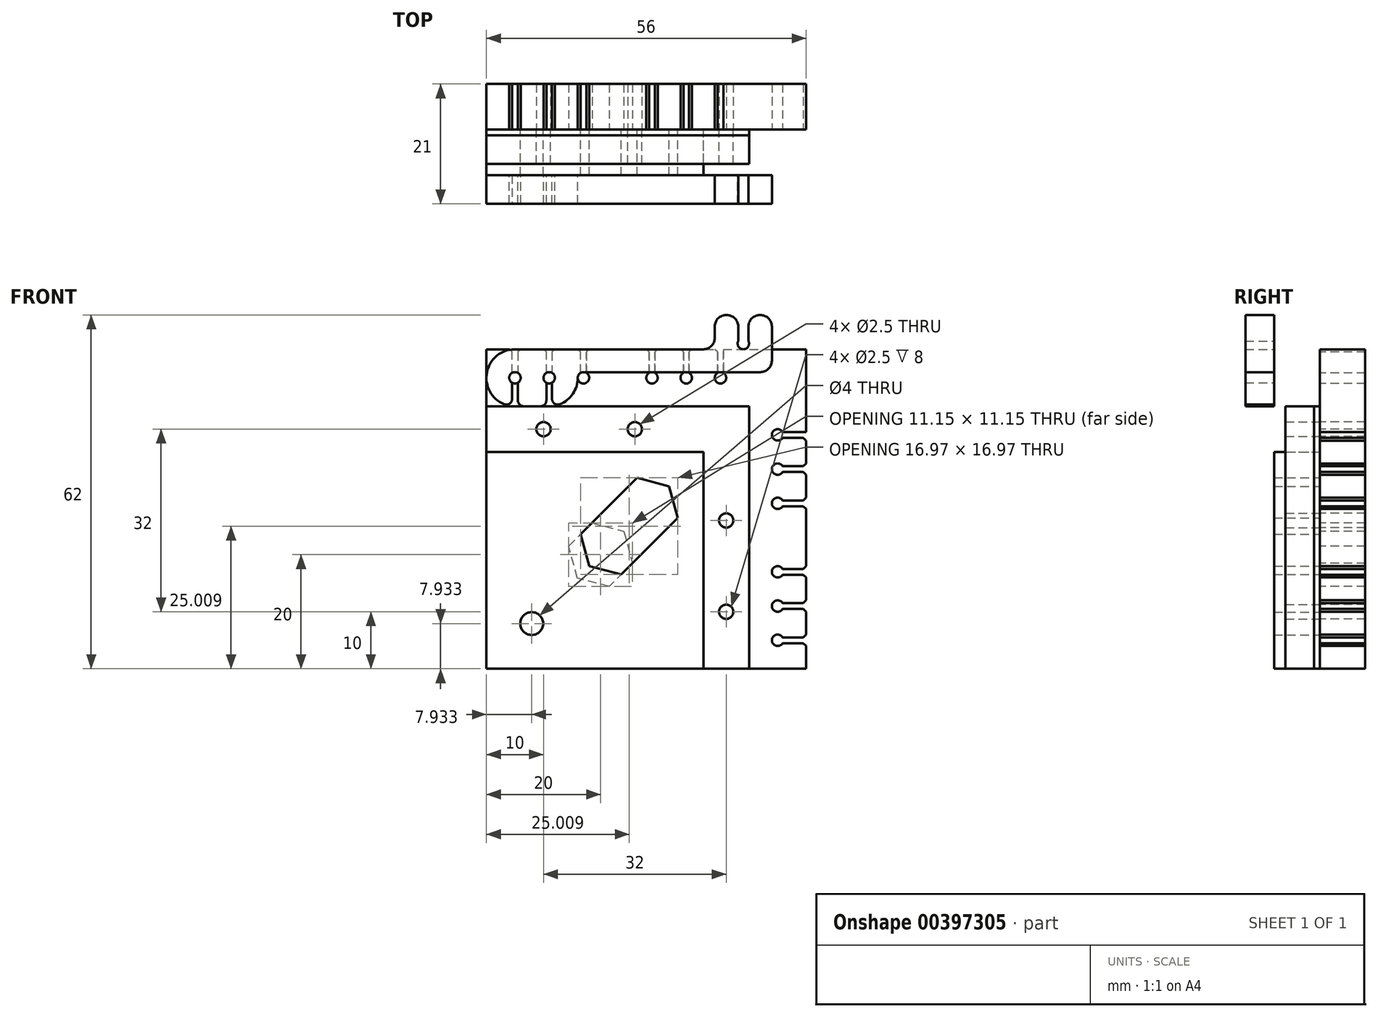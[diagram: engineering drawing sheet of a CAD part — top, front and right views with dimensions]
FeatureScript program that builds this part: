
annotation { "Feature Type Name" : "Feature", "Feature Type Description" : "" }
export const myFeature = defineFeature(function(context is Context, id is Id, definition is map)
    precondition{}
    {
        {
            assignVariable(context, id + "F0", {"name" : "Samm", "anyValue" : 4 * mm});
        }
        {
            assignVariable(context, id + "F1", {"name" : "Auk", "anyValue" : 2 * mm});
        }
        {
            assignVariable(context, id + "F2", {"name" : "Paksus", "anyValue" : getVariable(context, 'Samm') + getVariable(context, 'Auk') + getVariable(context, 'Samm') / 2});
        }
        {
            var Q0;
            Q0=qCreatedBy(makeId("Front.planeOp"),FACE);
            var sketch = newSketch(context, id + "F3", { "sketchPlane" : qUnion([Q0])});
            skLineSegment(sketch, "E0.bottom", {"start": v(0, 0) * mm, "end": v(56, 0) * mm});
            skLineSegment(sketch, "E0.top", {"start": v(0, 56) * mm, "end": v(56, 56) * mm});
            skLineSegment(sketch, "E0.left", {"start": v(0, 0) * mm, "end": v(0, 56) * mm});
            skLineSegment(sketch, "E0.right", {"start": v(56, 0) * mm, "end": v(56, 56) * mm});
            skLineSegment(sketch, "E1", {"start": v(0, 0) * mm, "end": v(56, 56) * mm});
            skLineSegment(sketch, "E2", {"start": v(0, 46) * mm, "end": v(46, 46) * mm});
            skLineSegment(sketch, "E3", {"start": v(0, 38) * mm, "end": v(38, 38) * mm});
            skLineSegment(sketch, "E4", {"start": v(0, 51) * mm, "end": v(56, 51) * mm, "construction": true});
            skLineSegment(sketch, "E5", {"start": v(46, 46) * mm, "end": v(46, 56) * mm, "construction": true});
            skLineSegment(sketch, "E6", {"start": v(38, 38) * mm, "end": v(38, 56) * mm, "construction": true});
            skLineSegment(sketch, "E7", {"start": v(0, 42) * mm, "end": v(42, 42) * mm, "construction": true});
            skPoint(sketch, "E8", {"position": v(26, 42) * mm});
            skPoint(sketch, "E9", {"position": v(10, 42) * mm});
            skSolve(sketch);
        }
        {
            var Q0;
            Q0=qCreatedBy(makeId("Front.planeOp"),FACE);
            var sketch = newSketch(context, id + "F4", { "sketchPlane" : qUnion([Q0])});
            skCircle(sketch, "E10", {"center": v(41, 51) * mm, "radius": 1 * mm});
            skCircle(sketch, "E11", {"center": v(35, 51) * mm, "radius": 1 * mm});
            skLineSegment(sketch, "E12", {"start": v(41.5, 56) * mm, "end": v(41.5, 51.87) * mm});
            skLineSegment(sketch, "E13.MirrorCS", {"start": v(40.5, 56) * mm, "end": v(40.5, 51.87) * mm});
            skLineSegment(sketch, "E14", {"start": v(40.5, 56) * mm, "end": v(41.5, 56) * mm});
            skCircle(sketch, "E15", {"center": v(29, 51) * mm, "radius": 1 * mm});
            skCircle(sketch, "E16", {"center": v(5, 51) * mm, "radius": 1 * mm});
            skLineSegment(sketch, "E17", {"start": v(5.5, 51.87) * mm, "end": v(5.5, 56) * mm});
            skLineSegment(sketch, "E18", {"start": v(5.5, 56) * mm, "end": v(4.5, 56) * mm});
            skLineSegment(sketch, "E19", {"start": v(4.5, 56) * mm, "end": v(4.5, 51.87) * mm});
            skCircle(sketch, "E20", {"center": v(11, 51) * mm, "radius": 1 * mm});
            skLineSegment(sketch, "E21", {"start": v(10.5, 56) * mm, "end": v(10.5, 51.87) * mm});
            skLineSegment(sketch, "E22", {"start": v(10.5, 56) * mm, "end": v(11.5, 56) * mm});
            skLineSegment(sketch, "E23", {"start": v(11.5, 51.87) * mm, "end": v(11.5, 56) * mm});
            skLineSegment(sketch, "E24", {"start": v(29.5, 51.87) * mm, "end": v(29.5, 56) * mm});
            skLineSegment(sketch, "E25", {"start": v(29.5, 56) * mm, "end": v(28.5, 56) * mm});
            skLineSegment(sketch, "E26", {"start": v(28.5, 56) * mm, "end": v(28.5, 51.87) * mm});
            skLineSegment(sketch, "E27", {"start": v(35.5, 51.87) * mm, "end": v(35.5, 56) * mm});
            skLineSegment(sketch, "E28", {"start": v(35.5, 56) * mm, "end": v(34.5, 56) * mm});
            skLineSegment(sketch, "E29", {"start": v(34.5, 56) * mm, "end": v(34.5, 51.87) * mm});
            skCircle(sketch, "E30", {"center": v(17, 51) * mm, "radius": 1 * mm});
            skLineSegment(sketch, "E31", {"start": v(16.5, 56) * mm, "end": v(16.5, 51.87) * mm});
            skLineSegment(sketch, "E32", {"start": v(16.5, 56) * mm, "end": v(17.5, 56) * mm});
            skLineSegment(sketch, "E33", {"start": v(17.5, 51.87) * mm, "end": v(17.5, 56) * mm});
            skSolve(sketch);
        }
        {
            var Q0;
            {var subQ3=sQuery(id+"F3.wireOp",EDGE,"E3");Q0=makeQuery(id+"F3.imprint","IMPRINT",FACE,{"disambiguationData":[TD([[makeQuery(id+"F3.imprint","IMPRINT",EDGE,{"derivedFrom":subQ3}),-1.0]])]});}
            var Q1;
            {var subQ0=sQuery(id+"F3.wireOp",EDGE,"E2");Q1=makeQuery(id+"F3.imprint","IMPRINT",FACE,{"disambiguationData":[TD([[makeQuery(id+"F3.imprint","IMPRINT",EDGE,{"derivedFrom":subQ0}),-1.0]])]});}
            var Q2;
            {var subQ7=sQuery(id+"F3.wireOp",EDGE,"E2");Q2=makeQuery(id+"F3.imprint","IMPRINT",FACE,{"disambiguationData":[TD([[makeQuery(id+"F3.imprint","IMPRINT",EDGE,{"derivedFrom":subQ7}),1.0]])]});}
            extrude(context, id + "F5", {"entities" : qUnion([Q0, Q1, Q2]), "oppositeDirection" : true, "depth" : 8 * mm});
        }
        {
            var Q0;
            {var subQ0=sQuery(id+"F3.wireOp",EDGE,"E2");Q0=makeQuery(id+"F3.imprint","IMPRINT",FACE,{"disambiguationData":[TD([[makeQuery(id+"F3.imprint","IMPRINT",EDGE,{"derivedFrom":subQ0}),-1.0]])]});}
            extrude(context, id + "F6", {"entities" : qUnion([Q0]), "depth" : 1 * mm});
        }
        {
            var Q0;
            {var subQ0=sQuery(id+"F4.wireOp",EDGE,"E16");var subQ1=makeQuery(id+"F4.imprint","INTERSECT",VERTEX,{"derivedFrom":[subQ0,sQuery(id+"F4.wireOp",EDGE,"E17")]});Q0=makeQuery(id+"F4.imprint","IMPRINT",FACE,{"disambiguationData":[TD([[makeQuery(id+"F4.imprint","IMPRINT",EDGE,{"disambiguationData":[TD([[subQ1,-1.0]])],"derivedFrom":subQ0}),1.0]])]});}
            var Q1;
            {var subQ0=sQuery(id+"F4.wireOp",EDGE,"E17");Q1=makeQuery(id+"F4.imprint","IMPRINT",FACE,{"disambiguationData":[TD([[makeQuery(id+"F4.imprint","IMPRINT",EDGE,{"derivedFrom":subQ0}),1.0]])]});}
            var Q2;
            {var subQ0=sQuery(id+"F4.wireOp",EDGE,"E20");var subQ1=makeQuery(id+"F4.imprint","INTERSECT",VERTEX,{"derivedFrom":[subQ0,sQuery(id+"F4.wireOp",EDGE,"E21")]});Q2=makeQuery(id+"F4.imprint","IMPRINT",FACE,{"disambiguationData":[TD([[makeQuery(id+"F4.imprint","IMPRINT",EDGE,{"disambiguationData":[TD([[subQ1,1.0]])],"derivedFrom":subQ0}),1.0]])]});}
            var Q3;
            {var subQ0=sQuery(id+"F4.wireOp",EDGE,"E21");Q3=makeQuery(id+"F4.imprint","IMPRINT",FACE,{"disambiguationData":[TD([[makeQuery(id+"F4.imprint","IMPRINT",EDGE,{"derivedFrom":subQ0}),1.0]])]});}
            var Q4;
            {var subQ0=sQuery(id+"F4.wireOp",EDGE,"QTqNx42c-BT7p-7A9X-RRYs-HgCFCDh2TXWR");Q4=makeQuery(id+"F4.imprint","IMPRINT",FACE,{"disambiguationData":[TD([[makeQuery(id+"F4.imprint","IMPRINT",EDGE,{"derivedFrom":subQ0}),1.0]])]});}
            var Q5;
            {var subQ0=sQuery(id+"F4.wireOp",EDGE,"DebvwMg3-Cwcg-wX2w-ogzT-Ep0VHspPX1UA");var subQ1=makeQuery(id+"F4.imprint","INTERSECT",VERTEX,{"derivedFrom":[subQ0,sQuery(id+"F4.wireOp",EDGE,"NG1M4aDK-SY8a-Geea-gYVj-s5fo7ngXQ215")]});Q5=makeQuery(id+"F4.imprint","IMPRINT",FACE,{"disambiguationData":[TD([[makeQuery(id+"F4.imprint","IMPRINT",EDGE,{"disambiguationData":[TD([[subQ1,-1.0]])],"derivedFrom":subQ0}),1.0]])]});}
            var Q6;
            {var subQ0=sQuery(id+"F4.wireOp",EDGE,"NG1M4aDK-SY8a-Geea-gYVj-s5fo7ngXQ215");Q6=makeQuery(id+"F4.imprint","IMPRINT",FACE,{"disambiguationData":[TD([[makeQuery(id+"F4.imprint","IMPRINT",EDGE,{"derivedFrom":subQ0}),1.0]])]});}
            var Q7;
            {var subQ0=sQuery(id+"F4.wireOp",EDGE,"E15");var subQ1=makeQuery(id+"F4.imprint","INTERSECT",VERTEX,{"derivedFrom":[subQ0,sQuery(id+"F4.wireOp",EDGE,"E24")]});Q7=makeQuery(id+"F4.imprint","IMPRINT",FACE,{"disambiguationData":[TD([[makeQuery(id+"F4.imprint","IMPRINT",EDGE,{"disambiguationData":[TD([[subQ1,-1.0]])],"derivedFrom":subQ0}),1.0]])]});}
            var Q8;
            {var subQ0=sQuery(id+"F4.wireOp",EDGE,"E24");Q8=makeQuery(id+"F4.imprint","IMPRINT",FACE,{"disambiguationData":[TD([[makeQuery(id+"F4.imprint","IMPRINT",EDGE,{"derivedFrom":subQ0}),1.0]])]});}
            var Q9;
            {var subQ0=sQuery(id+"F4.wireOp",EDGE,"E11");var subQ1=makeQuery(id+"F4.imprint","INTERSECT",VERTEX,{"derivedFrom":[subQ0,sQuery(id+"F4.wireOp",EDGE,"E27")]});Q9=makeQuery(id+"F4.imprint","IMPRINT",FACE,{"disambiguationData":[TD([[makeQuery(id+"F4.imprint","IMPRINT",EDGE,{"disambiguationData":[TD([[subQ1,-1.0]])],"derivedFrom":subQ0}),1.0]])]});}
            var Q10;
            {var subQ0=sQuery(id+"F4.wireOp",EDGE,"E27");Q10=makeQuery(id+"F4.imprint","IMPRINT",FACE,{"disambiguationData":[TD([[makeQuery(id+"F4.imprint","IMPRINT",EDGE,{"derivedFrom":subQ0}),1.0]])]});}
            var Q11;
            {var subQ0=sQuery(id+"F4.wireOp",EDGE,"E10");var subQ1=makeQuery(id+"F4.imprint","INTERSECT",VERTEX,{"derivedFrom":[subQ0,sQuery(id+"F4.wireOp",EDGE,"E12")]});Q11=makeQuery(id+"F4.imprint","IMPRINT",FACE,{"disambiguationData":[TD([[makeQuery(id+"F4.imprint","IMPRINT",EDGE,{"disambiguationData":[TD([[subQ1,-1.0]])],"derivedFrom":subQ0}),1.0]])]});}
            var Q12;
            {var subQ0=sQuery(id+"F4.wireOp",EDGE,"E12");Q12=makeQuery(id+"F4.imprint","IMPRINT",FACE,{"disambiguationData":[TD([[makeQuery(id+"F4.imprint","IMPRINT",EDGE,{"derivedFrom":subQ0}),-1.0]])]});}
            var Q13;
            {var subQ0=sQuery(id+"F4.wireOp",EDGE,"e30f7cc4-4558-49b8-8939-138344e96a64");Q13=makeQuery(id+"F4.imprint","IMPRINT",FACE,{"disambiguationData":[TD([[makeQuery(id+"F4.imprint","IMPRINT",EDGE,{"derivedFrom":subQ0}),-1.0]])]});}
            var Q14;
            {var subQ0=sQuery(id+"F4.wireOp",EDGE,"E31");Q14=makeQuery(id+"F4.imprint","IMPRINT",FACE,{"disambiguationData":[TD([[makeQuery(id+"F4.imprint","IMPRINT",EDGE,{"derivedFrom":subQ0}),1.0]])]});}
            var Q15;
            {var subQ0=sQuery(id+"F4.wireOp",EDGE,"E30");var subQ1=makeQuery(id+"F4.imprint","INTERSECT",VERTEX,{"derivedFrom":[subQ0,sQuery(id+"F4.wireOp",EDGE,"E31")]});Q15=makeQuery(id+"F4.imprint","IMPRINT",FACE,{"disambiguationData":[TD([[makeQuery(id+"F4.imprint","IMPRINT",EDGE,{"disambiguationData":[TD([[subQ1,1.0]])],"derivedFrom":subQ0}),1.0]])]});}
            extrude(context, id + "F7", {"entities" : qUnion([Q0, Q1, Q2, Q3, Q4, Q5, Q6, Q7, Q8, Q9, Q10, Q11, Q12, Q13, Q14, Q15]), "operationType" : NewBodyOperationType.REMOVE, "endBound" : BoundingType.UP_TO_NEXT, "oppositeDirection" : true, "depth" : 25 * mm});
        }
        {
            var Q0;
            Q0=makeQuery(id+"F7.boolean.opBoolean","COPY",EDGE,{"derivedFrom":makeQuery(id+"F7.opExtrude","SWEPT_EDGE",EDGE,{"disambiguationData":[OSD([sQuery(id+"F4.wireOp",EDGE,"E18"),sQuery(id+"F4.wireOp",EDGE,"E19")])]})});
            var Q1;
            Q1=makeQuery(id+"F7.boolean.opBoolean","COPY",EDGE,{"derivedFrom":makeQuery(id+"F7.opExtrude","SWEPT_EDGE",EDGE,{"disambiguationData":[OSD([sQuery(id+"F4.wireOp",EDGE,"E17"),sQuery(id+"F4.wireOp",EDGE,"E18")])]})});
            var Q2;
            Q2=makeQuery(id+"F7.boolean.opBoolean","COPY",EDGE,{"derivedFrom":makeQuery(id+"F7.opExtrude","SWEPT_EDGE",EDGE,{"disambiguationData":[OSD([sQuery(id+"F4.wireOp",EDGE,"E21"),sQuery(id+"F4.wireOp",EDGE,"E22")])]})});
            var Q3;
            Q3=makeQuery(id+"F7.boolean.opBoolean","COPY",EDGE,{"derivedFrom":makeQuery(id+"F7.opExtrude","SWEPT_EDGE",EDGE,{"disambiguationData":[OSD([sQuery(id+"F4.wireOp",EDGE,"E22"),sQuery(id+"F4.wireOp",EDGE,"E23")])]})});
            var Q4;
            Q4=makeQuery(id+"F7.boolean.opBoolean","COPY",EDGE,{"derivedFrom":makeQuery(id+"F7.opExtrude","SWEPT_EDGE",EDGE,{"disambiguationData":[OSD([sQuery(id+"F4.wireOp",EDGE,"E13.MirrorCS"),sQuery(id+"F4.wireOp",EDGE,"E14")])]})});
            var Q5;
            Q5=makeQuery(id+"F7.boolean.opBoolean","COPY",EDGE,{"derivedFrom":makeQuery(id+"F7.opExtrude","SWEPT_EDGE",EDGE,{"disambiguationData":[OSD([sQuery(id+"F4.wireOp",EDGE,"E12"),sQuery(id+"F4.wireOp",EDGE,"E14")])]})});
            var Q6;
            Q6=makeQuery(id+"F7.boolean.opBoolean","COPY",EDGE,{"derivedFrom":makeQuery(id+"F7.opExtrude","SWEPT_EDGE",EDGE,{"disambiguationData":[OSD([sQuery(id+"F4.wireOp",EDGE,"E27"),sQuery(id+"F4.wireOp",EDGE,"E28")])]})});
            var Q7;
            Q7=makeQuery(id+"F7.boolean.opBoolean","COPY",EDGE,{"derivedFrom":makeQuery(id+"F7.opExtrude","SWEPT_EDGE",EDGE,{"disambiguationData":[OSD([sQuery(id+"F4.wireOp",EDGE,"E28"),sQuery(id+"F4.wireOp",EDGE,"E29")])]})});
            var Q8;
            Q8=makeQuery(id+"F7.boolean.opBoolean","COPY",EDGE,{"derivedFrom":makeQuery(id+"F7.opExtrude","SWEPT_EDGE",EDGE,{"disambiguationData":[OSD([sQuery(id+"F4.wireOp",EDGE,"E24"),sQuery(id+"F4.wireOp",EDGE,"E25")])]})});
            var Q9;
            Q9=makeQuery(id+"F7.boolean.opBoolean","COPY",EDGE,{"derivedFrom":makeQuery(id+"F7.opExtrude","SWEPT_EDGE",EDGE,{"disambiguationData":[OSD([sQuery(id+"F4.wireOp",EDGE,"E25"),sQuery(id+"F4.wireOp",EDGE,"E26")])]})});
            var Q10;
            Q10=makeQuery(id+"F7.boolean.opBoolean","COPY",EDGE,{"derivedFrom":makeQuery(id+"F7.opExtrude","SWEPT_EDGE",EDGE,{"disambiguationData":[OSD([sQuery(id+"F4.wireOp",EDGE,"E31"),sQuery(id+"F4.wireOp",EDGE,"E32")])]})});
            var Q11;
            Q11=makeQuery(id+"F7.boolean.opBoolean","COPY",EDGE,{"derivedFrom":makeQuery(id+"F7.opExtrude","SWEPT_EDGE",EDGE,{"disambiguationData":[OSD([sQuery(id+"F4.wireOp",EDGE,"E32"),sQuery(id+"F4.wireOp",EDGE,"E33")])]})});
            chamfer(context, id + "F8", {"entities" : qUnion([Q0, Q1, Q2, Q3, Q4, Q5, Q6, Q7, Q8, Q9, Q10, Q11]), "width" : 0.5 * mm, "tangentPropagation" : true});
        }
        {
            var Q0;
            Q0=sQuery(id+"F3.wireOp",VERTEX,"E9");
            var Q1;
            Q1=sQuery(id+"F3.wireOp",VERTEX,"E8");
            var Q2;
            Q2=makeQuery(id+"F5.opExtrude","SWEPT_BODY",BODY,{"disambiguationData":[OSD([sQuery(id+"F3.wireOp",EDGE,"E0.top"),sQuery(id+"F3.wireOp",EDGE,"E0.left"),sQuery(id+"F3.wireOp",EDGE,"E1")])]});
            hole(context, id + "F9", {"style" : HoleStyle.SIMPLE, "endStyle" : HoleEndStyle.THROUGH, "holeDiameter" : 2.5 * mm, "isTappedThrough" : true, "tappedDepth" : 12 * mm, "tapClearance" : 3, "locations" : qUnion([Q0, Q1]), "scope" : qUnion([Q2])});
        }
        {
            var Q0;
            Q0=makeQuery(id+"F5.opExtrude","SWEPT_BODY",BODY,{"disambiguationData":[OSD([sQuery(id+"F3.wireOp",EDGE,"E0.top"),sQuery(id+"F3.wireOp",EDGE,"E0.left"),sQuery(id+"F3.wireOp",EDGE,"E1")])]});
            var Q1;
            Q1=makeQuery(id+"F5.opExtrude","SWEPT_FACE",FACE,{"disambiguationData":[OSD([sQuery(id+"F3.wireOp",EDGE,"E1")])]});
            mirror(context, id + "F10", {"operationType" : NewBodyOperationType.ADD, "entities" : qUnion([Q0]), "mirrorPlane" : qUnion([Q1])});
        }
        {
            var Q0;
            Q0=makeQuery(id+"F6.opExtrude","SWEPT_BODY",BODY,{"disambiguationData":[OSD([sQuery(id+"F3.wireOp",EDGE,"E0.left"),sQuery(id+"F3.wireOp",EDGE,"E1"),sQuery(id+"F3.wireOp",EDGE,"E2"),sQuery(id+"F3.wireOp",EDGE,"E3")])]});
            var Q1;
            Q1=makeQuery(id+"F6.opExtrude","SWEPT_FACE",FACE,{"disambiguationData":[OSD([sQuery(id+"F3.wireOp",EDGE,"E1")])]});
            mirror(context, id + "F11", {"operationType" : NewBodyOperationType.ADD, "entities" : qUnion([Q0]), "mirrorPlane" : qUnion([Q1])});
        }
        {
            var Q0;
            {var subQ3=sQuery(id+"F3.wireOp",EDGE,"E3");Q0=makeQuery(id+"F3.imprint","IMPRINT",FACE,{"disambiguationData":[TD([[makeQuery(id+"F3.imprint","IMPRINT",EDGE,{"derivedFrom":subQ3}),-1.0]])]});}
            var sketch = newSketch(context, id + "F12", { "sketchPlane" : qUnion([Q0])});
            skLineSegment(sketch, "E34.0", {"start": v(0, 38) * mm, "end": v(38, 38) * mm});
            skLineSegment(sketch, "E35.0", {"start": v(38, 0) * mm, "end": v(38, 38) * mm});
            skLineSegment(sketch, "E36.0", {"start": v(0, 0) * mm, "end": v(0, 56) * mm});
            skLineSegment(sketch, "E37.0", {"start": v(0, 0) * mm, "end": v(56, 0) * mm});
            skLineSegment(sketch, "E38.0", {"start": v(0, 0) * mm, "end": v(56, 56) * mm});
            skLineSegment(sketch, "E39", {"start": v(32, 32) * mm, "end": v(26.42, 33.5) * mm});
            skLineSegment(sketch, "E40", {"start": v(26.42, 33.5) * mm, "end": v(16.52, 23.6) * mm});
            skLineSegment(sketch, "E41", {"start": v(16.52, 23.6) * mm, "end": v(18.02, 18.02) * mm});
            skLineSegment(sketch, "E42.MirrorCS", {"start": v(23.6, 16.52) * mm, "end": v(18.02, 18.02) * mm});
            skLineSegment(sketch, "E43.MirrorCS", {"start": v(32, 32) * mm, "end": v(33.5, 26.42) * mm});
            skLineSegment(sketch, "E44.MirrorCS", {"start": v(33.5, 26.42) * mm, "end": v(23.6, 16.52) * mm});
            skPoint(sketch, "E45", {"position": v(7.93, 7.93) * mm});
            skSolve(sketch);
        }
        {
            var Q0;
            Q0=qSketchRegion(id+"F12",true);
            extrude(context, id + "F13", {"entities" : qUnion([Q0]), "depth" : getVariable(context, 'Paksus')});
        }
        {
            var Q0;
            Q0=makeQuery(id+"F13.opExtrude","CAP_FACE",FACE,{"disambiguationData":[OSD([sQuery(id+"F12.wireOp",EDGE,"E34.0"),sQuery(id+"F12.wireOp",EDGE,"E35.0"),sQuery(id+"F12.wireOp",EDGE,"E36.0"),sQuery(id+"F12.wireOp",EDGE,"E37.0"),sQuery(id+"F12.wireOp",EDGE,"2cf8d3c9-5500-4004-992a-a7f99b6d44c5.0"),sQuery(id+"F12.wireOp",EDGE,"2cf8d3c9-5500-4004-992a-a7f99b6d44c5.1"),sQuery(id+"F12.wireOp",EDGE,"2cf8d3c9-5500-4004-992a-a7f99b6d44c5.2"),sQuery(id+"F12.wireOp",EDGE,"2cf8d3c9-5500-4004-992a-a7f99b6d44c5.3"),sQuery(id+"F12.wireOp",EDGE,"2cf8d3c9-5500-4004-992a-a7f99b6d44c5.4"),sQuery(id+"F12.wireOp",EDGE,"2cf8d3c9-5500-4004-992a-a7f99b6d44c5.5")])],"isStart":false});
            var sketch = newSketch(context, id + "F14", { "sketchPlane" : qUnion([Q0])});
            skCircle(sketch, "E46.0", {"center": v(5, 51) * mm, "radius": 1 * mm});
            skCircle(sketch, "E47.0", {"center": v(11, 51) * mm, "radius": 1 * mm});
            skCircle(sketch, "E48.0", {"center": v(41, 51) * mm, "radius": 1 * mm});
            skCircle(sketch, "E49", {"center": v(11, 51) * mm, "radius": 5 * mm});
            skCircle(sketch, "E50", {"center": v(5, 51) * mm, "radius": 5 * mm});
            skLineSegment(sketch, "E51.0", {"start": v(0, 51) * mm, "end": v(56, 51) * mm, "construction": true});
            skCircle(sketch, "E52", {"center": v(45, 57) * mm, "radius": 1 * mm});
            skLineSegment(sketch, "E53", {"start": v(50, 52) * mm, "end": v(15.9, 52) * mm});
            skLineSegment(sketch, "E54", {"start": v(4.5, 50.13) * mm, "end": v(4.5, 46.03) * mm});
            skLineSegment(sketch, "E55", {"start": v(5.5, 50.13) * mm, "end": v(5.5, 46.03) * mm});
            skLineSegment(sketch, "E56", {"start": v(10.5, 50.13) * mm, "end": v(10.5, 46.03) * mm});
            skLineSegment(sketch, "E57", {"start": v(11.5, 50.13) * mm, "end": v(11.5, 46.03) * mm});
            skLineSegment(sketch, "E58", {"start": v(5.5, 46.03) * mm, "end": v(10.5, 46.03) * mm});
            skLineSegment(sketch, "E59.0", {"start": v(46, 46) * mm, "end": v(46, 56) * mm, "construction": true});
            skLineSegment(sketch, "E60", {"start": v(45.9, 57.44) * mm, "end": v(45.9, 62) * mm});
            skLineSegment(sketch, "E61", {"start": v(44.1, 57.44) * mm, "end": v(44.1, 62) * mm});
            skLineSegment(sketch, "E62", {"start": v(50, 52) * mm, "end": v(50, 62) * mm});
            skLineSegment(sketch, "E63", {"start": v(50, 62) * mm, "end": v(40, 62) * mm});
            skLineSegment(sketch, "E64", {"start": v(40, 62) * mm, "end": v(40, 56) * mm});
            skLineSegment(sketch, "E65", {"start": v(40, 56) * mm, "end": v(5, 56) * mm});
            skPoint(sketch, "E66.orphan", {"position": v(0, 62) * mm});
            skPoint(sketch, "E67.start.orphan", {"position": v(0, 56) * mm});
            skSolve(sketch);
        }
        {
            var Q0;
            {var subQ0=sQuery(id+"F14.wireOp",EDGE,"E56");Q0=makeQuery(id+"F14.imprint","IMPRINT",FACE,{"disambiguationData":[TD([[makeQuery(id+"F14.imprint","IMPRINT",EDGE,{"derivedFrom":subQ0}),-1.0]])]});}
            var Q1;
            {var subQ0=sQuery(id+"F14.wireOp",EDGE,"AxJx2oVJ-XFwZ-MC76-LPeR-xshG9jsGcbUg");var subQ1=sQuery(id+"F14.wireOp",EDGE,"E49");var subQ2=makeQuery(id+"F14.imprint","INTERSECT",VERTEX,{"derivedFrom":[subQ1,subQ0]});Q1=makeQuery(id+"F14.imprint","IMPRINT",FACE,{"disambiguationData":[TD([[makeQuery(id+"F14.imprint","IMPRINT",EDGE,{"disambiguationData":[TD([[subQ2,-1.0]])],"derivedFrom":subQ1}),-1.0]])]});}
            var Q2;
            {var subQ0=sQuery(id+"F14.wireOp",EDGE,"E58");Q2=makeQuery(id+"F14.imprint","IMPRINT",FACE,{"disambiguationData":[TD([[makeQuery(id+"F14.imprint","IMPRINT",EDGE,{"derivedFrom":subQ0}),1.0]])]});}
            var Q3;
            {var subQ0=sQuery(id+"F14.wireOp",EDGE,"CSsFTJs7-Jaks-gvLE-uZ3l-TUTck8eSOqBI");Q3=makeQuery(id+"F14.imprint","IMPRINT",FACE,{"disambiguationData":[TD([[makeQuery(id+"F14.imprint","IMPRINT",EDGE,{"derivedFrom":subQ0}),-1.0]])]});}
            var Q4;
            {var subQ2=sQuery(id+"F14.wireOp",EDGE,"E54");Q4=makeQuery(id+"F14.imprint","IMPRINT",FACE,{"disambiguationData":[TD([[makeQuery(id+"F14.imprint","IMPRINT",EDGE,{"derivedFrom":subQ2}),-1.0]])]});}
            var Q5;
            {var subQ2=sQuery(id+"F14.wireOp",EDGE,"E57");Q5=makeQuery(id+"F14.imprint","IMPRINT",FACE,{"disambiguationData":[TD([[makeQuery(id+"F14.imprint","IMPRINT",EDGE,{"derivedFrom":subQ2}),1.0]])]});}
            var Q6;
            {var subQ6=sQuery(id+"F14.wireOp",EDGE,"E60");var subQ8=sQuery(id+"F14.wireOp",EDGE,"E52");var subQ9=makeQuery(id+"F14.imprint","INTERSECT",VERTEX,{"derivedFrom":[subQ8,subQ6]});Q6=makeQuery(id+"F14.imprint","IMPRINT",FACE,{"disambiguationData":[TD([[makeQuery(id+"F14.imprint","IMPRINT",EDGE,{"disambiguationData":[TD([[subQ9,1.0]])],"derivedFrom":subQ8}),-1.0]])]});}
            var Q7;
            {var subQ0=sQuery(id+"F14.wireOp",EDGE,"E55");Q7=makeQuery(id+"F14.imprint","IMPRINT",FACE,{"disambiguationData":[TD([[makeQuery(id+"F14.imprint","IMPRINT",EDGE,{"derivedFrom":subQ0}),1.0]])]});}
            var Q8;
            {var subQ0=sQuery(id+"F14.wireOp",EDGE,"E55");Q8=makeQuery(id+"F14.imprint","IMPRINT",FACE,{"disambiguationData":[TD([[makeQuery(id+"F14.imprint","IMPRINT",EDGE,{"derivedFrom":subQ0}),1.0]])]});}
            var Q9;
            {var subQ0=sQuery(id+"F14.wireOp",EDGE,"E56");Q9=makeQuery(id+"F14.imprint","IMPRINT",FACE,{"disambiguationData":[TD([[makeQuery(id+"F14.imprint","IMPRINT",EDGE,{"derivedFrom":subQ0}),-1.0]])]});}
            var Q10;
            {var subQ0=sQuery(id+"F14.wireOp",EDGE,"E53");var subQ1=sQuery(id+"F14.wireOp",EDGE,"E49");var subQ2=makeQuery(id+"F14.imprint","INTERSECT",VERTEX,{"derivedFrom":[subQ1,subQ0]});Q10=makeQuery(id+"F14.imprint","IMPRINT",FACE,{"disambiguationData":[TD([[makeQuery(id+"F14.imprint","IMPRINT",EDGE,{"disambiguationData":[TD([[subQ2,-1.0]])],"derivedFrom":subQ1}),-1.0]])]});}
            var Q11;
            {var subQ0=sQuery(id+"F14.wireOp",EDGE,"E49");var subQ1=makeQuery(id+"F14.imprint","INTERSECT",VERTEX,{"derivedFrom":[sQuery(id+"F14.wireOp",EDGE,"E46.0"),subQ0]});Q11=makeQuery(id+"F14.imprint","IMPRINT",FACE,{"disambiguationData":[TD([[makeQuery(id+"F14.imprint","IMPRINT",EDGE,{"disambiguationData":[TD([[subQ1,1.0]])],"derivedFrom":subQ0}),1.0]])]});}
            var Q12;
            {var subQ0=sQuery(id+"F14.wireOp",EDGE,"E49");var subQ1=makeQuery(id+"F14.imprint","INTERSECT",VERTEX,{"derivedFrom":[sQuery(id+"F14.wireOp",EDGE,"E46.0"),subQ0]});Q12=makeQuery(id+"F14.imprint","IMPRINT",FACE,{"disambiguationData":[TD([[makeQuery(id+"F14.imprint","IMPRINT",EDGE,{"disambiguationData":[TD([[subQ1,1.0]])],"derivedFrom":subQ0}),1.0]])]});}
            var Q13;
            {var subQ2=sQuery(id+"F14.wireOp",EDGE,"E54");Q13=makeQuery(id+"F14.imprint","IMPRINT",FACE,{"disambiguationData":[TD([[makeQuery(id+"F14.imprint","IMPRINT",EDGE,{"derivedFrom":subQ2}),-1.0]])]});}
            var Q14;
            {var subQ0=sQuery(id+"F14.wireOp",EDGE,"BxTuXfEc-kO9Q-QHb8-LTs3-kqM6wV0efrVW");var subQ1=sQuery(id+"F14.wireOp",EDGE,"E48.0");var subQ2=makeQuery(id+"F14.imprint","INTERSECT",VERTEX,{"derivedFrom":[subQ1,subQ0]});Q14=makeQuery(id+"F14.imprint","IMPRINT",FACE,{"disambiguationData":[TD([[makeQuery(id+"F14.imprint","IMPRINT",EDGE,{"disambiguationData":[TD([[subQ2,-1.0]])],"derivedFrom":subQ1}),-1.0]])]});}
            extrude(context, id + "F15", {"entities" : qUnion([Q0, Q1, Q2, Q3, Q4, Q5, Q6, Q7, Q8, Q9, Q10, Q11, Q12, Q13, Q14]), "depth" : 5 * mm});
        }
        {
            var Q0;
            Q0=makeQuery(id+"F15.opExtrude","SWEPT_EDGE",EDGE,{"disambiguationData":[OSD([sQuery(id+"F14.wireOp",EDGE,"E50"),sQuery(id+"F14.wireOp",EDGE,"E54")])]});
            var Q1;
            Q1=makeQuery(id+"F15.opExtrude","SWEPT_EDGE",EDGE,{"disambiguationData":[OSD([sQuery(id+"F14.wireOp",EDGE,"E50"),sQuery(id+"F14.wireOp",EDGE,"E55"),sQuery(id+"F14.wireOp",EDGE,"E58")])]});
            var Q2;
            Q2=makeQuery(id+"F15.opExtrude","SWEPT_EDGE",EDGE,{"disambiguationData":[OSD([sQuery(id+"F14.wireOp",EDGE,"E49"),sQuery(id+"F14.wireOp",EDGE,"E56"),sQuery(id+"F14.wireOp",EDGE,"E58")])]});
            var Q3;
            Q3=makeQuery(id+"F15.opExtrude","SWEPT_EDGE",EDGE,{"disambiguationData":[OSD([sQuery(id+"F14.wireOp",EDGE,"E49"),sQuery(id+"F14.wireOp",EDGE,"E57")])]});
            var Q4;
            Q4=makeQuery(id+"F15.opExtrude","SWEPT_EDGE",EDGE,{"disambiguationData":[OSD([sQuery(id+"F14.wireOp",EDGE,"AxJx2oVJ-XFwZ-MC76-LPeR-xshG9jsGcbUg"),sQuery(id+"F14.wireOp",EDGE,"ckgy3OCV-uk7f-uJ41-MpvO-jaV0Tc8mXzn0")])]});
            var Q5;
            Q5=makeQuery(id+"F15.opExtrude","SWEPT_EDGE",EDGE,{"disambiguationData":[OSD([sQuery(id+"F14.wireOp",EDGE,"AxJx2oVJ-XFwZ-MC76-LPeR-xshG9jsGcbUg"),sQuery(id+"F14.wireOp",EDGE,"Tde4fxld-xR9Y-IW79-mpMQ-LUkHlr8zzJhR")])]});
            var Q6;
            Q6=makeQuery(id+"F15.opExtrude","SWEPT_EDGE",EDGE,{"disambiguationData":[OSD([sQuery(id+"F14.wireOp",EDGE,"E49"),sQuery(id+"F14.wireOp",EDGE,"E53")])]});
            fillet(context, id + "F16", {"entities" : qUnion([Q0, Q1, Q2, Q3, Q4, Q5, Q6]), "radius" : 1 * mm, "tangentPropagation" : true, "allowEdgeOverflow" : false});
        }
        {
            var Q0;
            Q0=sQuery(id+"F12.wireOp",VERTEX,"E45");
            var Q1;
            Q1=makeQuery(id+"F13.opExtrude","SWEPT_BODY",BODY,{"disambiguationData":[OSD([sQuery(id+"F12.wireOp",EDGE,"E34.0"),sQuery(id+"F12.wireOp",EDGE,"E35.0"),sQuery(id+"F12.wireOp",EDGE,"E36.0"),sQuery(id+"F12.wireOp",EDGE,"E37.0"),sQuery(id+"F12.wireOp",EDGE,"E39"),sQuery(id+"F12.wireOp",EDGE,"E40"),sQuery(id+"F12.wireOp",EDGE,"E41"),sQuery(id+"F12.wireOp",EDGE,"E42.MirrorCS"),sQuery(id+"F12.wireOp",EDGE,"E44.MirrorCS"),sQuery(id+"F12.wireOp",EDGE,"E43.MirrorCS")])]});
            hole(context, id + "F17", {"style" : HoleStyle.SIMPLE, "endStyle" : HoleEndStyle.THROUGH, "oppositeDirection" : true, "holeDiameter" : 4 * mm, "isTappedThrough" : true, "tappedDepth" : 12 * mm, "tapClearance" : 3, "locations" : qUnion([Q0]), "scope" : qUnion([Q1])});
        }
        {
            var Q0;
            Q0=makeQuery(id+"F15.opExtrude","SWEPT_EDGE",EDGE,{"disambiguationData":[OSD([sQuery(id+"F14.wireOp",EDGE,"E64"),sQuery(id+"F14.wireOp",EDGE,"E65")])]});
            var Q1;
            Q1=makeQuery(id+"F15.opExtrude","SWEPT_EDGE",EDGE,{"disambiguationData":[OSD([sQuery(id+"F14.wireOp",EDGE,"E63"),sQuery(id+"F14.wireOp",EDGE,"E64")])]});
            var Q2;
            Q2=makeQuery(id+"F15.opExtrude","SWEPT_EDGE",EDGE,{"disambiguationData":[OSD([sQuery(id+"F14.wireOp",EDGE,"E61"),sQuery(id+"F14.wireOp",EDGE,"E63")])]});
            var Q3;
            Q3=makeQuery(id+"F15.opExtrude","SWEPT_EDGE",EDGE,{"disambiguationData":[OSD([sQuery(id+"F14.wireOp",EDGE,"E60"),sQuery(id+"F14.wireOp",EDGE,"E63")])]});
            var Q4;
            Q4=makeQuery(id+"F15.opExtrude","SWEPT_EDGE",EDGE,{"disambiguationData":[OSD([sQuery(id+"F14.wireOp",EDGE,"E62"),sQuery(id+"F14.wireOp",EDGE,"E63")])]});
            var Q5;
            Q5=makeQuery(id+"F15.opExtrude","SWEPT_EDGE",EDGE,{"disambiguationData":[OSD([sQuery(id+"F14.wireOp",EDGE,"E53"),sQuery(id+"F14.wireOp",EDGE,"E62")])]});
            fillet(context, id + "F18", {"entities" : qUnion([Q0, Q1, Q2, Q3, Q4, Q5]), "radius" : 2 * mm, "tangentPropagation" : true, "allowEdgeOverflow" : false});
        }
        {
            var Q0;
            {var subQ3=sQuery(id+"F3.wireOp",EDGE,"E0.bottom");Q0=makeQuery(id+"F3.imprint","IMPRINT",FACE,{"disambiguationData":[TD([[makeQuery(id+"F3.imprint","IMPRINT",EDGE,{"derivedFrom":subQ3}),1.0]])]});}
            var sketch = newSketch(context, id + "F19", { "sketchPlane" : qUnion([Q0])});
            skCircle(sketch, "E68.cCircle", {"center": v(20, 20) * mm, "radius": 5.77 * mm, "construction": true});
            skLineSegment(sketch, "E68.0", {"start": v(25.58, 18.5) * mm, "end": v(21.5, 14.42) * mm});
            skLineSegment(sketch, "E68.1", {"start": v(21.5, 14.42) * mm, "end": v(15.92, 15.92) * mm});
            skLineSegment(sketch, "E68.2", {"start": v(15.92, 15.92) * mm, "end": v(14.42, 21.5) * mm});
            skLineSegment(sketch, "E68.3", {"start": v(14.42, 21.5) * mm, "end": v(18.5, 25.58) * mm});
            skLineSegment(sketch, "E68.4", {"start": v(18.5, 25.58) * mm, "end": v(24.08, 24.08) * mm});
            skLineSegment(sketch, "E68.5", {"start": v(24.08, 24.08) * mm, "end": v(25.58, 18.5) * mm});
            skSolve(sketch);
        }
        {
            var Q0;
            Q0=makeQuery(id+"F19.imprint","IMPRINT",FACE,{"disambiguationData":[TD([[makeQuery(id+"F19.imprint","IMPRINT",EDGE,{"derivedFrom":sQuery(id+"F19.wireOp",EDGE,"E68.0")}),-1.0]])]});
            var Q1;
            {var subQ0=sQuery(id+"F19.wireOp",EDGE,"E68.2");Q1=makeQuery(id+"F19.imprint","IMPRINT",FACE,{"disambiguationData":[TD([[makeQuery(id+"F19.imprint","IMPRINT",EDGE,{"derivedFrom":subQ0}),-1.0]])]});}
            extrude(context, id + "F20", {"entities" : qUnion([Q0, Q1]), "operationType" : NewBodyOperationType.REMOVE, "endBound" : BoundingType.UP_TO_NEXT, "oppositeDirection" : true, "depth" : 25 * mm});
        }
        {
            var Q0;
            {var subQ3=sQuery(id+"F3.wireOp",EDGE,"E0.bottom");Q0=makeQuery(id+"F3.imprint","IMPRINT",FACE,{"disambiguationData":[TD([[makeQuery(id+"F3.imprint","IMPRINT",EDGE,{"derivedFrom":subQ3}),1.0]])]});}
            var sketch = newSketch(context, id + "F21", { "sketchPlane" : qUnion([Q0])});
            skLineSegment(sketch, "E69.bottom", {"start": v(0, 0) * mm, "end": v(46, 0) * mm});
            skLineSegment(sketch, "E69.top", {"start": v(0, 46) * mm, "end": v(46, 46) * mm});
            skLineSegment(sketch, "E69.left", {"start": v(0, 0) * mm, "end": v(0, 46) * mm});
            skLineSegment(sketch, "E69.right", {"start": v(46, 0) * mm, "end": v(46, 46) * mm});
            skCircle(sketch, "E70.0", {"center": v(10, 42) * mm, "radius": 1.25 * mm});
            skCircle(sketch, "E71.0", {"center": v(26, 42) * mm, "radius": 1.25 * mm});
            skCircle(sketch, "E72.0", {"center": v(42, 26) * mm, "radius": 1.25 * mm});
            skCircle(sketch, "E73.0", {"center": v(42, 10) * mm, "radius": 1.25 * mm});
            skSolve(sketch);
        }
        {
            var Q0;
            Q0 = qSketchRegion(id + "F21", true);
            extrude(context, id + "F22", {"entities" : qUnion([Q0]), "depth" : 6 * mm});
        }
    });
